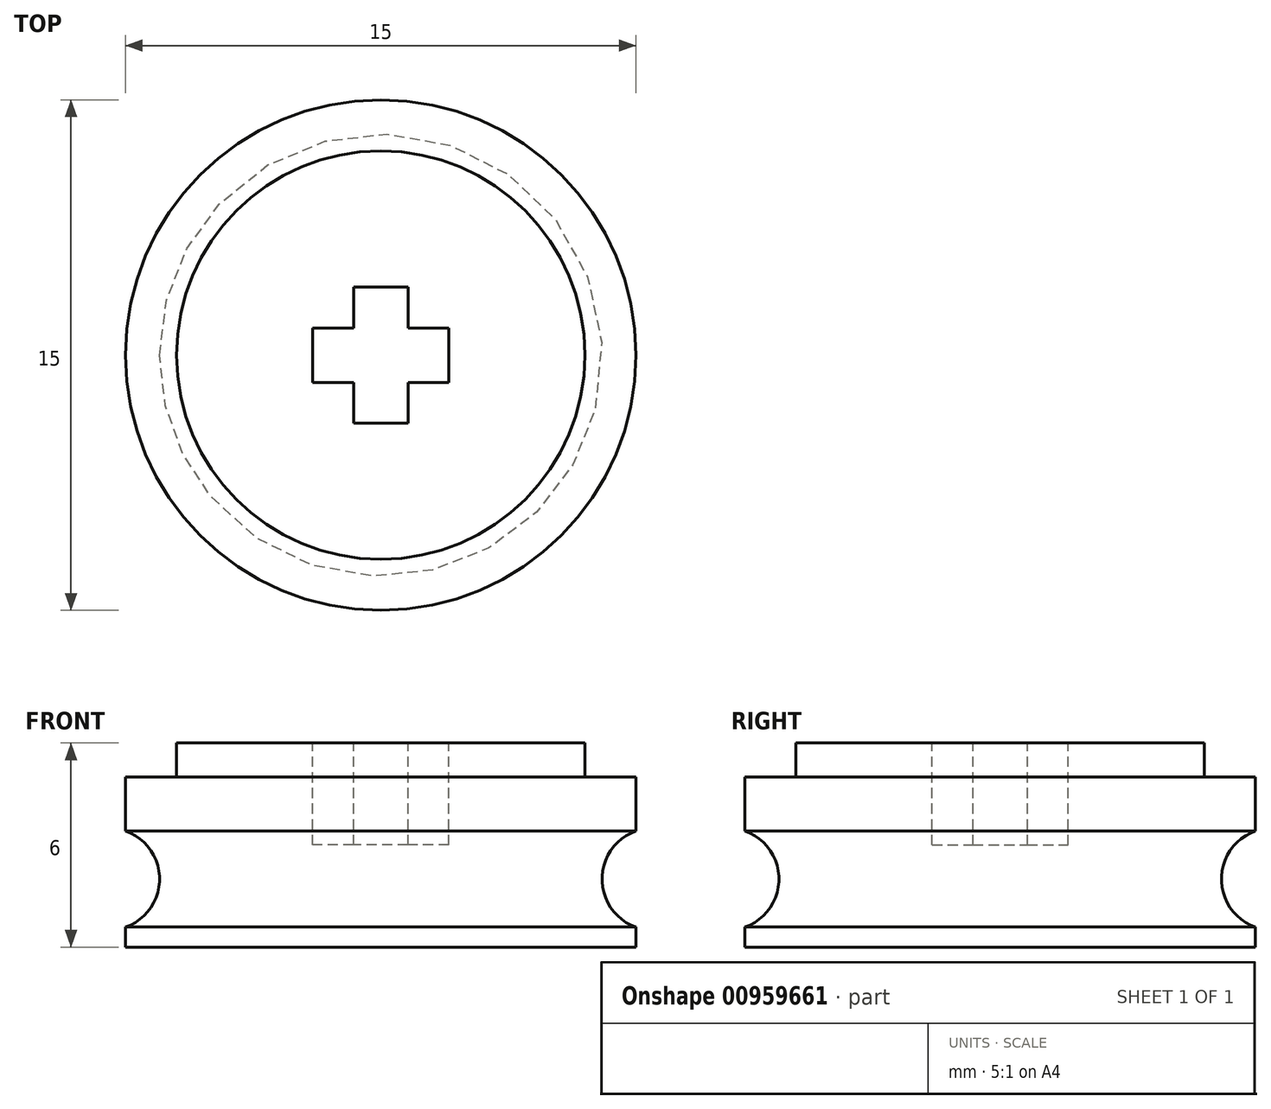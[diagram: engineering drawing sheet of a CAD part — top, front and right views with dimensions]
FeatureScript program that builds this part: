
annotation { "Feature Type Name" : "Feature", "Feature Type Description" : "" }
export const myFeature = defineFeature(function(context is Context, id is Id, definition is map)
    precondition{}
    {
        {
            var Q0;
            Q0=qCreatedBy(makeId("Top.planeOp"),FACE);
            var sketch = newSketch(context, id + "F0", { "sketchPlane" : qUnion([Q0])});
            skCircle(sketch, "E0", {"center": v(0, 0) * mm, "radius": 7.5 * mm});
            skSolve(sketch);
        }
        {
            var Q0;
            Q0=makeQuery(id+"F0.imprint","IMPRINT",FACE,{"disambiguationData":[TD([[makeQuery(id+"F0.imprint","IMPRINT",EDGE,{"derivedFrom":sQuery(id+"F0.wireOp",EDGE,"E0")}),1.0]])]});
            extrude(context, id + "F1", {"entities" : qUnion([Q0]), "depth" : 5 * mm, "offsetDistance" : 25 * mm});
        }
        {
            var Q0;
            Q0=makeQuery(id+"F1.opExtrude","CAP_FACE",FACE,{"disambiguationData":[OSD([sQuery(id+"F0.wireOp",EDGE,"E0")])],"isStart":false});
            var sketch = newSketch(context, id + "F2", { "sketchPlane" : qUnion([Q0])});
            skCircle(sketch, "E1", {"center": v(0, 0) * mm, "radius": 6 * mm});
            skSolve(sketch);
        }
        {
            var Q0;
            Q0 = qSketchRegion(id + "F2", true);
            extrude(context, id + "F3", {"entities" : qUnion([Q0]), "operationType" : NewBodyOperationType.ADD, "depth" : 1 * mm, "offsetDistance" : 25 * mm});
        }
        {
            var Q0;
            Q0=makeQuery(id+"F3.opExtrude","CAP_FACE",FACE,{"disambiguationData":[OSD([sQuery(id+"F2.wireOp",EDGE,"E1")])],"isStart":false});
            var sketch = newSketch(context, id + "F4", { "sketchPlane" : qUnion([Q0])});
            skLineSegment(sketch, "E2.bottom", {"start": v(2, -0.8) * mm, "end": v(-2, -0.8) * mm});
            skLineSegment(sketch, "E2.top", {"start": v(2, 0.8) * mm, "end": v(-2, 0.8) * mm});
            skLineSegment(sketch, "E2.left", {"start": v(2, -0.8) * mm, "end": v(2, 0.8) * mm});
            skLineSegment(sketch, "E2.right", {"start": v(-2, -0.8) * mm, "end": v(-2, 0.8) * mm});
            skPoint(sketch, "E2.middle", {"position": v(0, 0) * mm});
            skLineSegment(sketch, "E3.bottom", {"start": v(0.8, -2) * mm, "end": v(-0.8, -2) * mm});
            skLineSegment(sketch, "E3.top", {"start": v(0.8, 2) * mm, "end": v(-0.8, 2) * mm});
            skLineSegment(sketch, "E3.left", {"start": v(0.8, -2) * mm, "end": v(0.8, 2) * mm});
            skLineSegment(sketch, "E3.right", {"start": v(-0.8, -2) * mm, "end": v(-0.8, 2) * mm});
            skSolve(sketch);
        }
        {
            var Q0;
            {var subQ5=sQuery(id+"F4.wireOp",EDGE,"E3.top");Q0=makeQuery(id+"F4.imprint","IMPRINT",FACE,{"disambiguationData":[TD([[makeQuery(id+"F4.imprint","IMPRINT",EDGE,{"derivedFrom":subQ5}),1.0]])]});}
            var Q1;
            {var subQ0=sQuery(id+"F4.wireOp",EDGE,"E2.right");Q1=makeQuery(id+"F4.imprint","IMPRINT",FACE,{"disambiguationData":[TD([[makeQuery(id+"F4.imprint","IMPRINT",EDGE,{"derivedFrom":subQ0}),-1.0]])]});}
            var Q2;
            {var subQ0=sQuery(id+"F4.wireOp",EDGE,"E3.left");var subQ1=sQuery(id+"F4.wireOp",EDGE,"E2.bottom");var subQ2=makeQuery(id+"F4.imprint","INTERSECT",VERTEX,{"derivedFrom":[subQ1,subQ0]});Q2=makeQuery(id+"F4.imprint","IMPRINT",FACE,{"disambiguationData":[TD([[makeQuery(id+"F4.imprint","IMPRINT",EDGE,{"disambiguationData":[TD([[subQ2,-1.0]])],"derivedFrom":subQ1}),-1.0]])]});}
            var Q3;
            {var subQ0=sQuery(id+"F4.wireOp",EDGE,"E2.left");Q3=makeQuery(id+"F4.imprint","IMPRINT",FACE,{"disambiguationData":[TD([[makeQuery(id+"F4.imprint","IMPRINT",EDGE,{"derivedFrom":subQ0}),1.0]])]});}
            var Q4;
            {var subQ5=sQuery(id+"F4.wireOp",EDGE,"E3.bottom");Q4=makeQuery(id+"F4.imprint","IMPRINT",FACE,{"disambiguationData":[TD([[makeQuery(id+"F4.imprint","IMPRINT",EDGE,{"derivedFrom":subQ5}),-1.0]])]});}
            extrude(context, id + "F5", {"entities" : qUnion([Q0, Q1, Q2, Q3, Q4]), "operationType" : NewBodyOperationType.REMOVE, "oppositeDirection" : true, "depth" : 3 * mm, "offsetDistance" : 25 * mm});
        }
        {
            var Q0;
            Q0=qCreatedBy(makeId("Front.planeOp"),FACE);
            var sketch = newSketch(context, id + "F6", { "sketchPlane" : qUnion([Q0])});
            skLineSegment(sketch, "E4", {"start": v(0, 21.61) * mm, "end": v(0, -17.13) * mm, "construction": true});
            skSolve(sketch);
        }
        {
            var Q0;
            Q0=qCreatedBy(makeId("Right.planeOp"),FACE);
            var sketch = newSketch(context, id + "F7", { "sketchPlane" : qUnion([Q0])});
            skCircle(sketch, "E5", {"center": v(-8, 2) * mm, "radius": 1.5 * mm});
            skSolve(sketch);
        }
        {
            var Q0;
            Q0=makeQuery(id+"F7.imprint","IMPRINT",FACE,{"disambiguationData":[TD([[makeQuery(id+"F7.imprint","IMPRINT",EDGE,{"derivedFrom":sQuery(id+"F7.wireOp",EDGE,"E5")}),1.0]])]});
            var Q1;
            Q1=sQuery(id+"F6.wireOp",EDGE,"E4");
            revolve(context, id + "F8", {"operationType" : NewBodyOperationType.REMOVE, "surfaceOperationType" : NewSurfaceOperationType.NEW, "entities" : qUnion([Q0]), "axis" : qUnion([Q1]), "revolveType" : RevolveType.FULL, "oppositeDirection" : true});
        }
    });
